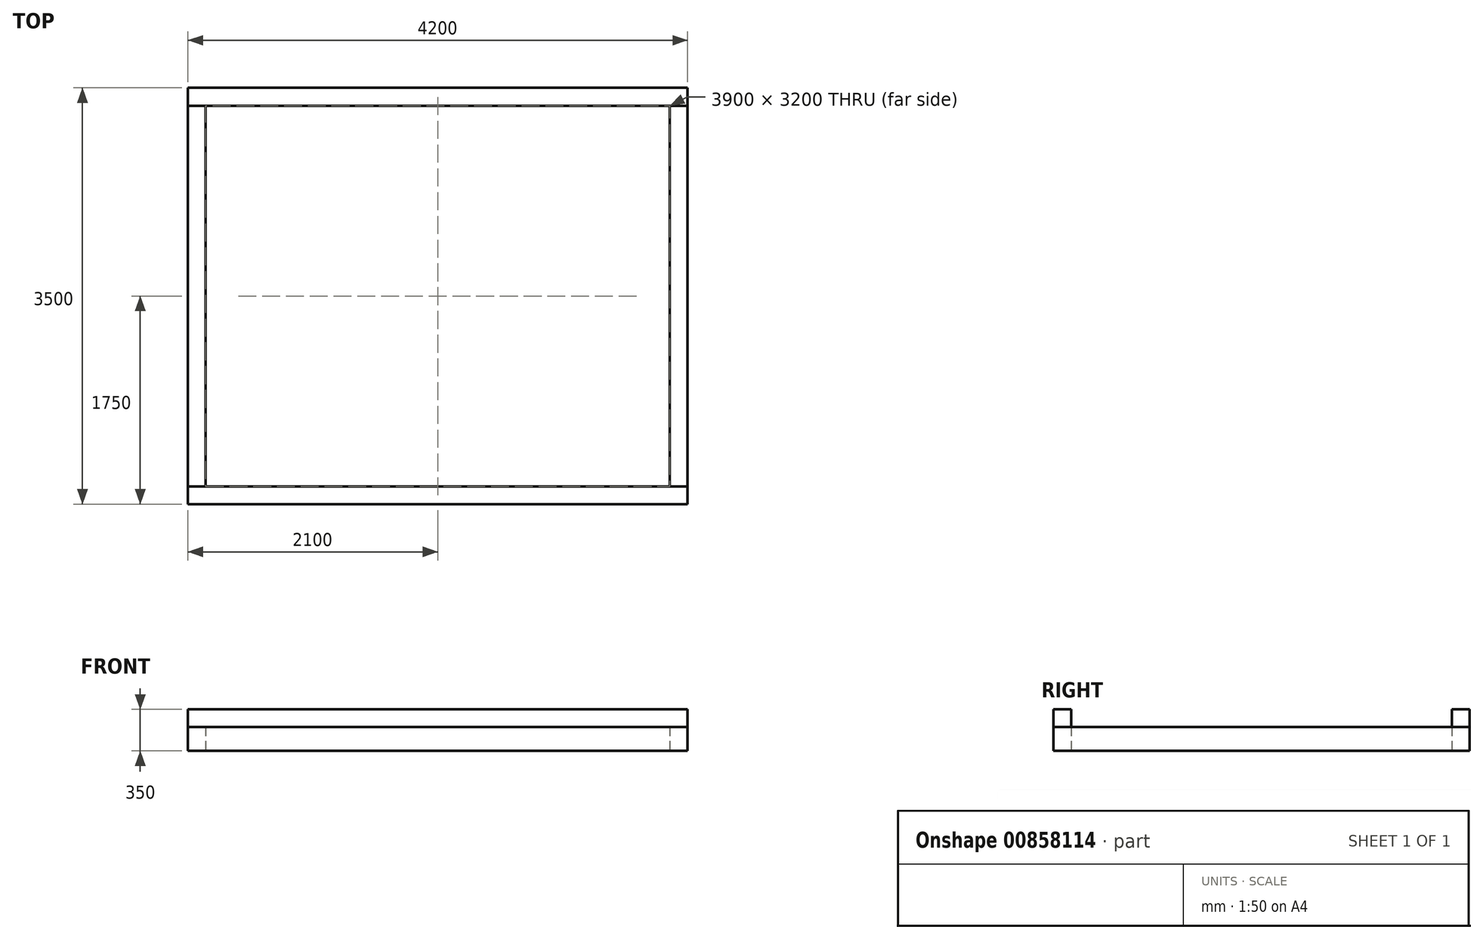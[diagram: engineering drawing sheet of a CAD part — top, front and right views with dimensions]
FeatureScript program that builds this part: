
annotation { "Feature Type Name" : "Feature", "Feature Type Description" : "" }
export const myFeature = defineFeature(function(context is Context, id is Id, definition is map)
    precondition{}
    {
        {
            var Q0;
            Q0=qCreatedBy(makeId("Top.planeOp"),FACE);
            var sketch = newSketch(context, id + "F0", { "sketchPlane" : qUnion([Q0])});
            skLineSegment(sketch, "E0.bottom", {"start": v(0, 0) * mm, "end": v(4200, 0) * mm});
            skLineSegment(sketch, "E0.top", {"start": v(0, 3500) * mm, "end": v(4200, 3500) * mm});
            skLineSegment(sketch, "E0.left", {"start": v(0, 0) * mm, "end": v(0, 3500) * mm});
            skLineSegment(sketch, "E0.right", {"start": v(4200, 0) * mm, "end": v(4200, 3500) * mm});
            skLineSegment(sketch, "E1.bottom", {"start": v(150, 3350) * mm, "end": v(4050, 3350) * mm});
            skLineSegment(sketch, "E1.top", {"start": v(150, 150) * mm, "end": v(4050, 150) * mm});
            skLineSegment(sketch, "E1.left", {"start": v(150, 3350) * mm, "end": v(150, 150) * mm});
            skLineSegment(sketch, "E1.right", {"start": v(4050, 3350) * mm, "end": v(4050, 150) * mm});
            skSolve(sketch);
        }
        {
            var Q0;
            Q0 = qSketchRegion(id + "F0", true);
            extrude(context, id + "F1", {"entities" : qUnion([Q0]), "depth" : 200 * mm, "offsetDistance" : 25.4 * mm});
        }
        {
            var Q0;
            Q0=makeQuery(id+"F1.opExtrude","SWEPT_FACE",FACE,{"disambiguationData":[OSD([sQuery(id+"F0.wireOp",EDGE,"E0.right")])]});
            var sketch = newSketch(context, id + "F2", { "sketchPlane" : qUnion([Q0])});
            skLineSegment(sketch, "E2.bottom", {"start": v(0, 200) * mm, "end": v(150, 200) * mm});
            skLineSegment(sketch, "E2.top", {"start": v(0, 350) * mm, "end": v(150, 350) * mm});
            skLineSegment(sketch, "E2.left", {"start": v(0, 200) * mm, "end": v(0, 350) * mm});
            skLineSegment(sketch, "E2.right", {"start": v(150, 200) * mm, "end": v(150, 350) * mm});
            skLineSegment(sketch, "E3.bottom", {"start": v(3500, 200) * mm, "end": v(3350, 200) * mm});
            skLineSegment(sketch, "E3.top", {"start": v(3500, 350) * mm, "end": v(3350, 350) * mm});
            skLineSegment(sketch, "E3.left", {"start": v(3500, 200) * mm, "end": v(3500, 350) * mm});
            skLineSegment(sketch, "E3.right", {"start": v(3350, 200) * mm, "end": v(3350, 350) * mm});
            skSolve(sketch);
        }
        {
            var Q0;
            Q0 = qSketchRegion(id + "F2", true);
            extrude(context, id + "F3", {"entities" : qUnion([Q0]), "oppositeDirection" : true, "depth" : 4200 * mm, "offsetDistance" : 25.4 * mm});
        }
    });
